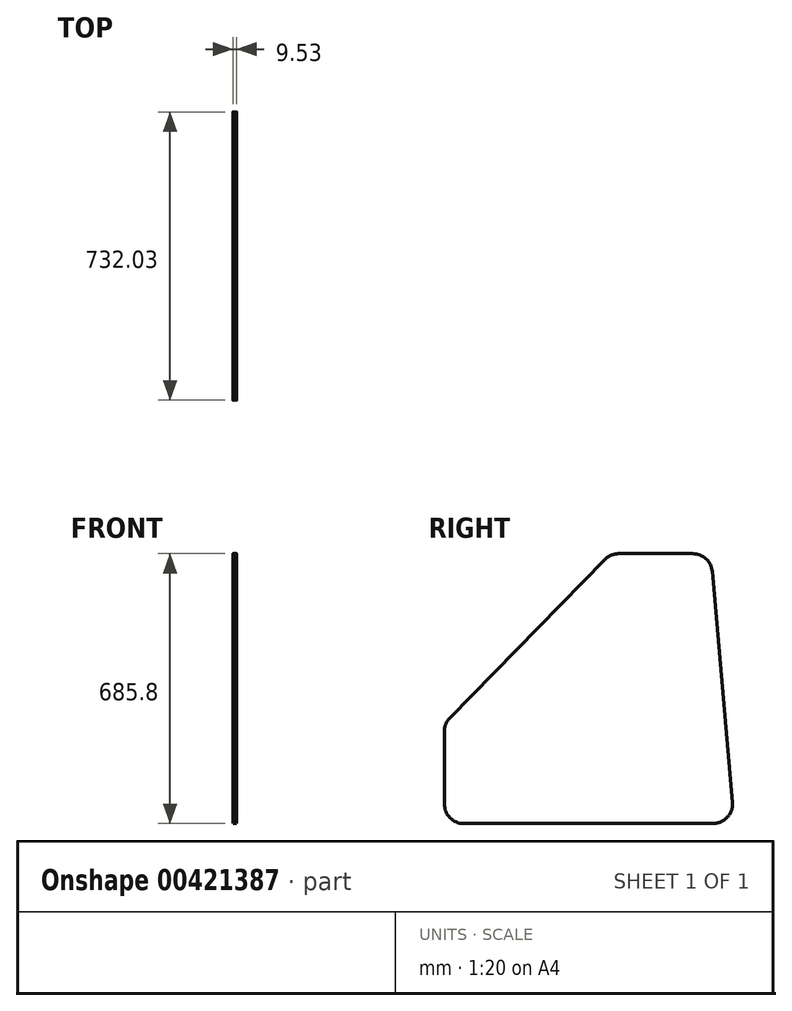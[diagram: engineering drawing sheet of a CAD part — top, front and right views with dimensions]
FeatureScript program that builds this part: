
annotation { "Feature Type Name" : "Feature", "Feature Type Description" : "" }
export const myFeature = defineFeature(function(context is Context, id is Id, definition is map)
    precondition{}
    {
        {
            var Q0;
            Q0=qCreatedBy(makeId("Right.planeOp"),FACE);
            var sketch = newSketch(context, id + "F0", { "sketchPlane" : qUnion([Q0])});
            skLineSegment(sketch, "E0", {"start": v(-54.57, 0) * mm, "end": v(-686.6, 0) * mm});
            skLineSegment(sketch, "E1", {"start": v(-736.6, 50) * mm, "end": v(-736.6, 233.6) * mm});
            skLineSegment(sketch, "E2", {"start": v(-722.33, 268.58) * mm, "end": v(-328.7, 670.77) * mm});
            skLineSegment(sketch, "E3", {"start": v(-56, 640.16) * mm, "end": v(-4.76, 54.36) * mm});
            skLineSegment(sketch, "E4", {"start": v(-292.97, 685.8) * mm, "end": v(-105.82, 685.8) * mm});
            skPoint(sketch, "E5.visualSharp", {"position": v(-60, 685.8) * mm});
            skArc(sketch, "E5.filletArc", {"start": v(-56, 640.16) * mm, "mid": v(-72.04, 672.66) * mm, "end": v(-105.82, 685.8) * mm});
            skPoint(sketch, "E6.visualSharp", {"position": v(-314, 685.8) * mm});
            skArc(sketch, "E6.filletArc", {"start": v(-292.97, 685.8) * mm, "mid": v(-312.36, 681.9) * mm, "end": v(-328.7, 670.77) * mm});
            skPoint(sketch, "E7.visualSharp", {"position": v(-736.6, 254) * mm});
            skArc(sketch, "E7.filletArc", {"start": v(-722.33, 268.58) * mm, "mid": v(-732.9, 252.49) * mm, "end": v(-736.6, 233.6) * mm});
            skPoint(sketch, "E8.visualSharp", {"position": v(-736.6, 0) * mm});
            skArc(sketch, "E8.filletArc", {"start": v(-736.6, 50) * mm, "mid": v(-721.96, 14.64) * mm, "end": v(-686.6, 0) * mm});
            skPoint(sketch, "E9.visualSharp", {"position": v(0, 0) * mm});
            skArc(sketch, "E9.filletArc", {"start": v(-54.57, 0) * mm, "mid": v(-17.7, 16.22) * mm, "end": v(-4.76, 54.36) * mm});
            skSolve(sketch);
        }
        {
            var Q0;
            Q0 = qSketchRegion(id + "F0", true);
            extrude(context, id + "F1", {"entities" : qUnion([Q0]), "depth" : 9.53 * mm});
        }
    });
